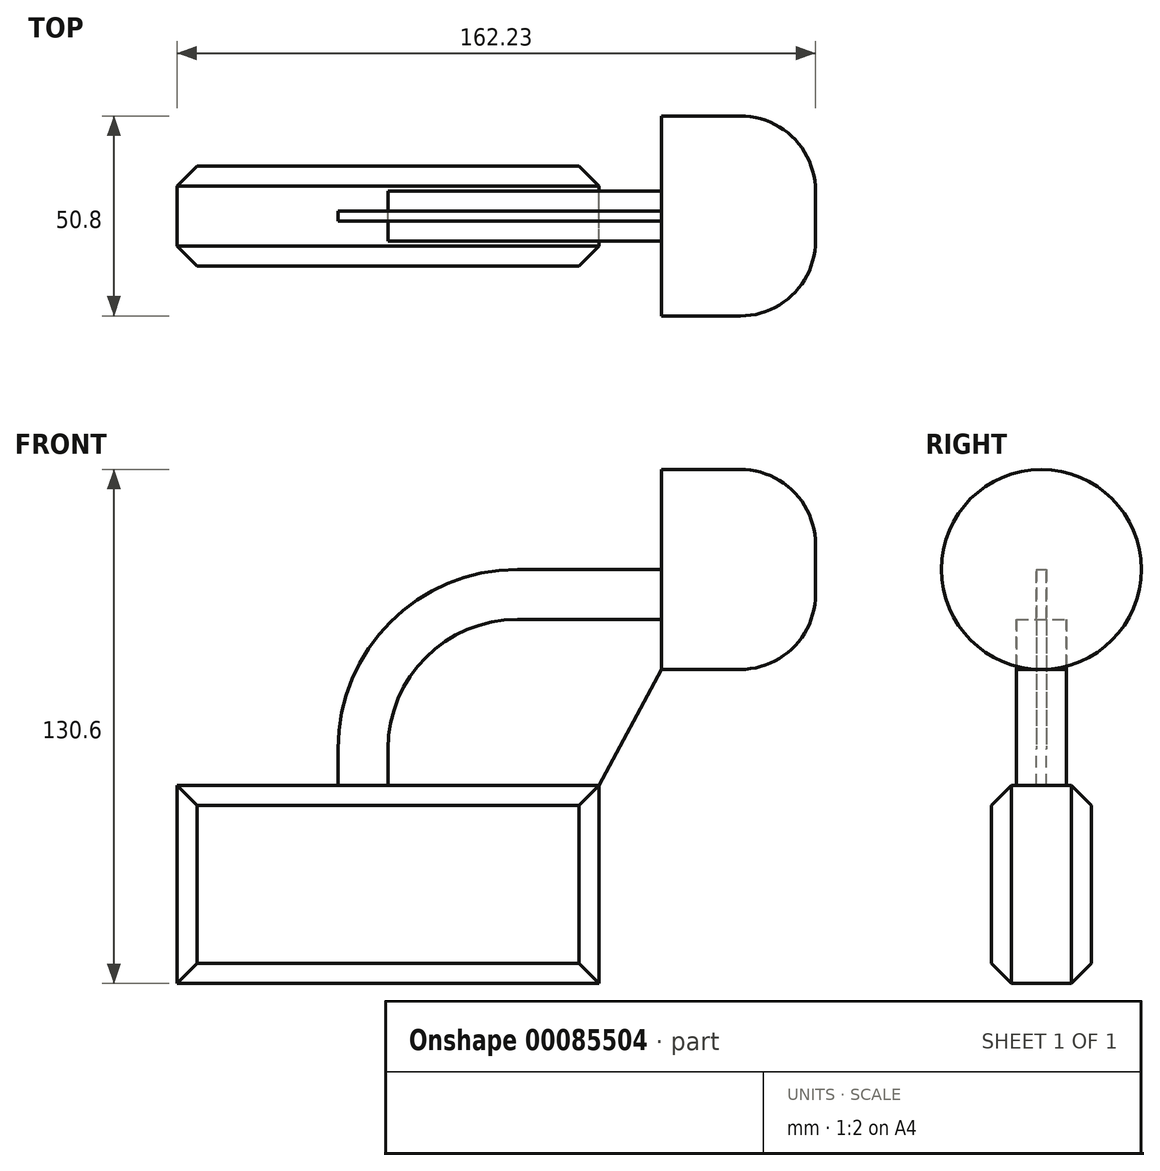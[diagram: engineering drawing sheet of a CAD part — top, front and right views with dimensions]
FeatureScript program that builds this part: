
annotation { "Feature Type Name" : "Feature", "Feature Type Description" : "" }
export const myFeature = defineFeature(function(context is Context, id is Id, definition is map)
    precondition{}
    {
        {
            var Q0;
            Q0=qCreatedBy(makeId("Front.planeOp"),FACE);
            var sketch = newSketch(context, id + "F0", { "sketchPlane" : qUnion([Q0])});
            skLineSegment(sketch, "E0.bottom", {"start": v(53.64, 25.14) * mm, "end": v(-53.64, 25.14) * mm});
            skLineSegment(sketch, "E0.top", {"start": v(53.64, -25.14) * mm, "end": v(-53.64, -25.14) * mm});
            skLineSegment(sketch, "E0.left", {"start": v(53.64, 25.14) * mm, "end": v(53.64, -25.14) * mm});
            skLineSegment(sketch, "E0.right", {"start": v(-53.64, 25.14) * mm, "end": v(-53.64, -25.14) * mm});
            skPoint(sketch, "E0.middle", {"position": v(0, 0) * mm});
            skLineSegment(sketch, "E1.bottom", {"start": v(69.42, 54.66) * mm, "end": v(108.6, 54.66) * mm});
            skLineSegment(sketch, "E1.top", {"start": v(69.42, 80.06) * mm, "end": v(108.6, 80.06) * mm});
            skLineSegment(sketch, "E1.left", {"start": v(69.42, 54.66) * mm, "end": v(69.42, 80.06) * mm});
            skLineSegment(sketch, "E1.right", {"start": v(108.6, 54.66) * mm, "end": v(108.6, 80.06) * mm});
            skPoint(sketch, "E1.middle", {"position": v(89, 67.36) * mm});
            skLineSegment(sketch, "E2", {"start": v(0, 0) * mm, "end": v(0, 34.5) * mm});
            skPoint(sketch, "E2.endSnap0", {"position": v(0, 25.14) * mm});
            skLineSegment(sketch, "E3", {"start": v(89, 67.36) * mm, "end": v(32.87, 67.36) * mm});
            skArc(sketch, "E4", {"start": v(0, 34.5) * mm, "mid": v(9.63, 57.73) * mm, "end": v(32.87, 67.36) * mm});
            skLineSegment(sketch, "E5", {"start": v(53.64, 25.14) * mm, "end": v(69.42, 54.66) * mm});
            skLineSegment(sketch, "E6.0", {"start": v(-12.7, 0) * mm, "end": v(-12.7, 34.5) * mm});
            skArc(sketch, "E6.1", {"start": v(-12.7, 34.5) * mm, "mid": v(0.65, 66.71) * mm, "end": v(32.87, 80.06) * mm});
            skLineSegment(sketch, "E6.2", {"start": v(89, 80.06) * mm, "end": v(32.87, 80.06) * mm});
            skSolve(sketch);
        }
        {
            var Q0;
            Q0=makeQuery(id+"F0.imprint","IMPRINT",FACE,{"disambiguationData":[TD([[makeQuery(id+"F0.imprint","IMPRINT",EDGE,{"derivedFrom":sQuery(id+"F0.wireOp",EDGE,"E0.top")}),-1.0]])]});
            extrude(context, id + "F1", {"entities" : qUnion([Q0]), "endBound" : BoundingType.SYMMETRIC, "depth" : 25.4 * mm});
        }
        {
            var Q0;
            {var subQ4=sQuery(id+"F0.wireOp",EDGE,"E1.bottom");Q0=makeQuery(id+"F0.imprint","IMPRINT",FACE,{"disambiguationData":[TD([[makeQuery(id+"F0.imprint","IMPRINT",EDGE,{"derivedFrom":subQ4}),1.0]])]});}
            var Q1;
            Q1=sQuery(id+"F0.wireOp",EDGE,"E1.top");
            revolve(context, id + "F2", {"entities" : qUnion([Q0]), "axis" : qUnion([Q1]), "revolveType" : RevolveType.FULL});
        }
        {
            var Q0;
            {var subQ0=sQuery(id+"F0.wireOp",EDGE,"E4");Q0=makeQuery(id+"F0.imprint","IMPRINT",FACE,{"disambiguationData":[TD([[makeQuery(id+"F0.imprint","IMPRINT",EDGE,{"derivedFrom":subQ0}),1.0]])]});}
            extrude(context, id + "F3", {"entities" : qUnion([Q0]), "endBound" : BoundingType.SYMMETRIC, "depth" : 12.7 * mm});
        }
        {
            var Q0;
            {var subQ0=sQuery(id+"F0.wireOp",EDGE,"E4");Q0=makeQuery(id+"F0.imprint","IMPRINT",FACE,{"disambiguationData":[TD([[makeQuery(id+"F0.imprint","IMPRINT",EDGE,{"derivedFrom":subQ0}),-1.0]])]});}
            extrude(context, id + "F4", {"entities" : qUnion([Q0]), "endBound" : BoundingType.SYMMETRIC, "depth" : 2.54 * mm});
        }
        {
            var Q0;
            Q0=makeQuery(id+"F2.opRevolve","SWEPT_EDGE",EDGE,{"disambiguationData":[OSD([sQuery(id+"F0.wireOp",EDGE,"E1.bottom"),sQuery(id+"F0.wireOp",EDGE,"E1.right")])]});
            fillet(context, id + "F5", {"entities" : qUnion([Q0]), "radius" : 19.05 * mm, "tangentPropagation" : true, "allowEdgeOverflow" : false});
        }
        {
            var Q0;
            Q0=makeQuery(id+"F1.opExtrude","CAP_EDGE",EDGE,{"disambiguationData":[OSD([sQuery(id+"F0.wireOp",EDGE,"E0.right")])],"isStart":false});
            var Q1;
            Q1=makeQuery(id+"F1.opExtrude","CAP_EDGE",EDGE,{"disambiguationData":[OSD([sQuery(id+"F0.wireOp",EDGE,"E0.bottom")])],"isStart":false});
            var Q2;
            Q2=makeQuery(id+"F1.opExtrude","CAP_EDGE",EDGE,{"disambiguationData":[OSD([sQuery(id+"F0.wireOp",EDGE,"E0.left")])],"isStart":false});
            var Q3;
            Q3=makeQuery(id+"F1.opExtrude","CAP_EDGE",EDGE,{"disambiguationData":[OSD([sQuery(id+"F0.wireOp",EDGE,"E0.top")])],"isStart":false});
            chamfer(context, id + "F6", {"entities" : qUnion([Q0, Q1, Q2, Q3]), "width" : 5.08 * mm, "tangentPropagation" : true});
        }
        {
            var Q0;
            Q0=makeQuery(id+"F1.opExtrude","CAP_EDGE",EDGE,{"disambiguationData":[OSD([sQuery(id+"F0.wireOp",EDGE,"E0.bottom")])],"isStart":true});
            var Q1;
            Q1=makeQuery(id+"F1.opExtrude","CAP_EDGE",EDGE,{"disambiguationData":[OSD([sQuery(id+"F0.wireOp",EDGE,"E0.left")])],"isStart":true});
            var Q2;
            Q2=makeQuery(id+"F1.opExtrude","CAP_EDGE",EDGE,{"disambiguationData":[OSD([sQuery(id+"F0.wireOp",EDGE,"E0.top")])],"isStart":true});
            var Q3;
            Q3=makeQuery(id+"F1.opExtrude","CAP_EDGE",EDGE,{"disambiguationData":[OSD([sQuery(id+"F0.wireOp",EDGE,"E0.right")])],"isStart":true});
            chamfer(context, id + "F7", {"entities" : qUnion([Q0, Q1, Q2, Q3]), "width" : 5.08 * mm, "tangentPropagation" : true});
        }
    });
